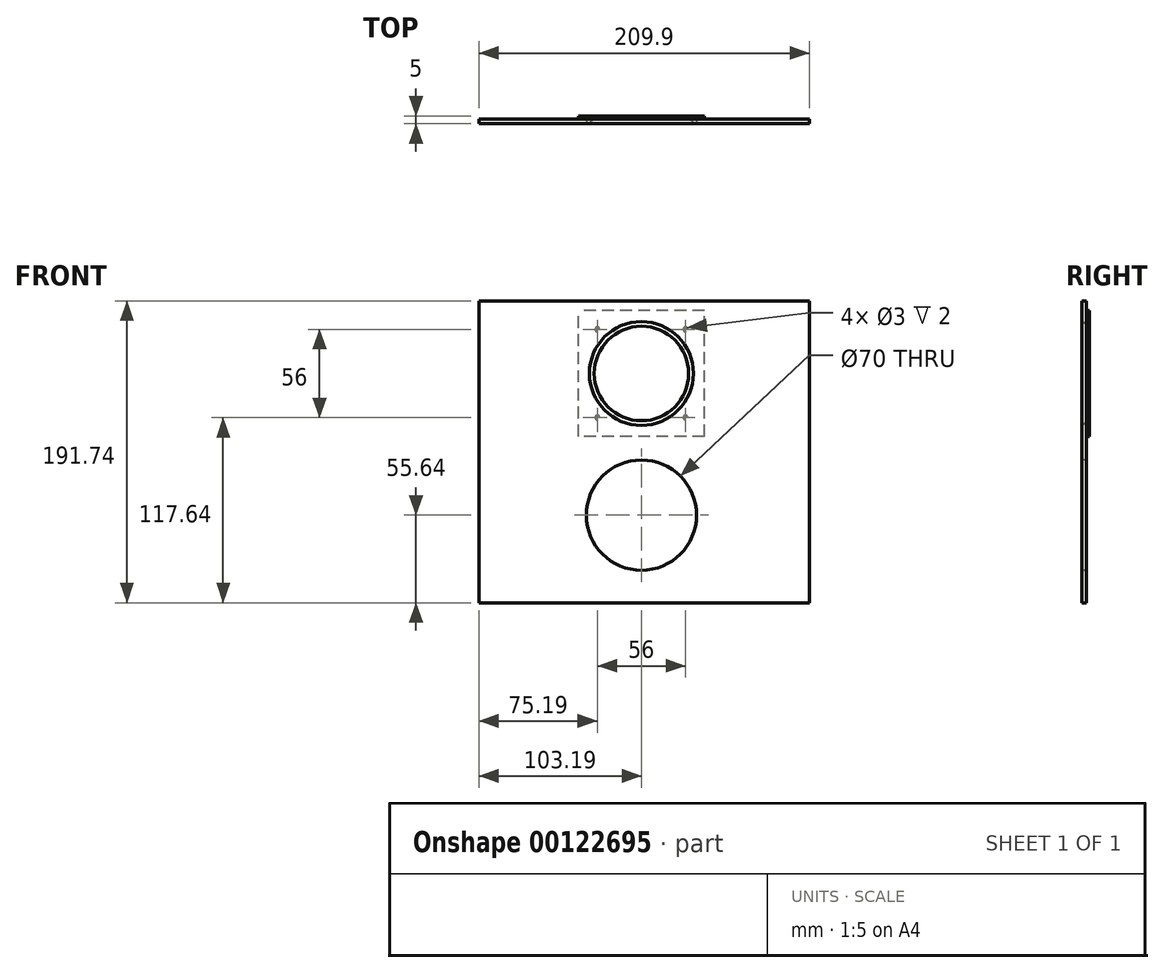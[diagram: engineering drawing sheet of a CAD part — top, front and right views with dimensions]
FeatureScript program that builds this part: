
annotation { "Feature Type Name" : "Feature", "Feature Type Description" : "" }
export const myFeature = defineFeature(function(context is Context, id is Id, definition is map)
    precondition{}
    {
        {
            var Q0;
            Q0=qCreatedBy(makeId("Front.planeOp"),FACE);
            cPlane(context, id + "F0", {"entities" : qUnion([Q0]), "cplaneType" : CPlaneType.OFFSET, "offset" : 5 * mm, "width" : 150 * mm, "height" : 150 * mm});
        }
        {
            var Q0;
            Q0=qCreatedBy(id+"F0.planeOp",FACE);
            var sketch = newSketch(context, id + "F1", { "sketchPlane" : qUnion([Q0])});
            skCircle(sketch, "E0", {"center": v(0, 0) * mm, "radius": 35 * mm});
            skCircle(sketch, "E1", {"center": v(0, -90) * mm, "radius": 35 * mm});
            skLineSegment(sketch, "E2.bottom", {"start": v(-103.2, 46.1) * mm, "end": v(106.7, 46.1) * mm});
            skLineSegment(sketch, "E2.top", {"start": v(-103.2, -145.64) * mm, "end": v(106.7, -145.64) * mm});
            skLineSegment(sketch, "E2.left", {"start": v(-103.2, 46.1) * mm, "end": v(-103.2, -145.64) * mm});
            skLineSegment(sketch, "E2.right", {"start": v(106.7, 46.1) * mm, "end": v(106.7, -145.64) * mm});
            skSolve(sketch);
        }
        {
            var Q0;
            Q0=qSketchRegion(id+"F1",true);
            extrude(context, id + "F2", {"entities" : qUnion([Q0]), "oppositeDirection" : true, "depth" : 3 * mm});
        }
        {
            var Q0;
            Q0=qCreatedBy(makeId("Right.planeOp"),FACE);
            var sketch = newSketch(context, id + "F3", { "sketchPlane" : qUnion([Q0])});
            skLineSegment(sketch, "E3", {"start": v(19.32, 0) * mm, "end": v(-16.11, 0) * mm, "construction": true});
            skLineSegment(sketch, "E4", {"start": v(-5, 35) * mm, "end": v(-5, 33) * mm});
            skLineSegment(sketch, "E5", {"start": v(-5, 33) * mm, "end": v(0, 30) * mm});
            skLineSegment(sketch, "E6", {"start": v(0, 30) * mm, "end": v(0, 35) * mm});
            skLineSegment(sketch, "E7", {"start": v(0, 35) * mm, "end": v(-5, 35) * mm});
            skSolve(sketch);
        }
        {
            var Q0;
            Q0=qSketchRegion(id+"F3",true);
            var Q1;
            Q1=sQuery(id+"F3.wireOp",EDGE,"E3");
            revolve(context, id + "F4", {"entities" : qUnion([Q0]), "axis" : qUnion([Q1]), "revolveType" : RevolveType.FULL});
        }
        {
            var Q0;
            Q0=qCreatedBy(makeId("Front.planeOp"),FACE);
            var sketch = newSketch(context, id + "F5", { "sketchPlane" : qUnion([Q0])});
            skCircle(sketch, "E8", {"center": v(0, 0) * mm, "radius": 35 * mm});
            skLineSegment(sketch, "E9.bottom", {"start": v(40, -40) * mm, "end": v(-40, -40) * mm});
            skLineSegment(sketch, "E9.top", {"start": v(40, 40) * mm, "end": v(-40, 40) * mm});
            skLineSegment(sketch, "E9.left", {"start": v(40, -40) * mm, "end": v(40, 40) * mm});
            skLineSegment(sketch, "E9.right", {"start": v(-40, -40) * mm, "end": v(-40, 40) * mm});
            skCircle(sketch, "E10", {"center": v(-28, 28) * mm, "radius": 1.5 * mm});
            skCircle(sketch, "E11", {"center": v(-28, -28) * mm, "radius": 1.5 * mm});
            skCircle(sketch, "E12", {"center": v(28, 28) * mm, "radius": 1.5 * mm});
            skCircle(sketch, "E13", {"center": v(28, -28) * mm, "radius": 1.5 * mm});
            skSolve(sketch);
        }
        {
            var Q0;
            Q0=qSketchRegion(id+"F5",true);
            extrude(context, id + "F6", {"entities" : qUnion([Q0]), "operationType" : NewBodyOperationType.ADD, "depth" : 2 * mm});
        }
    });
